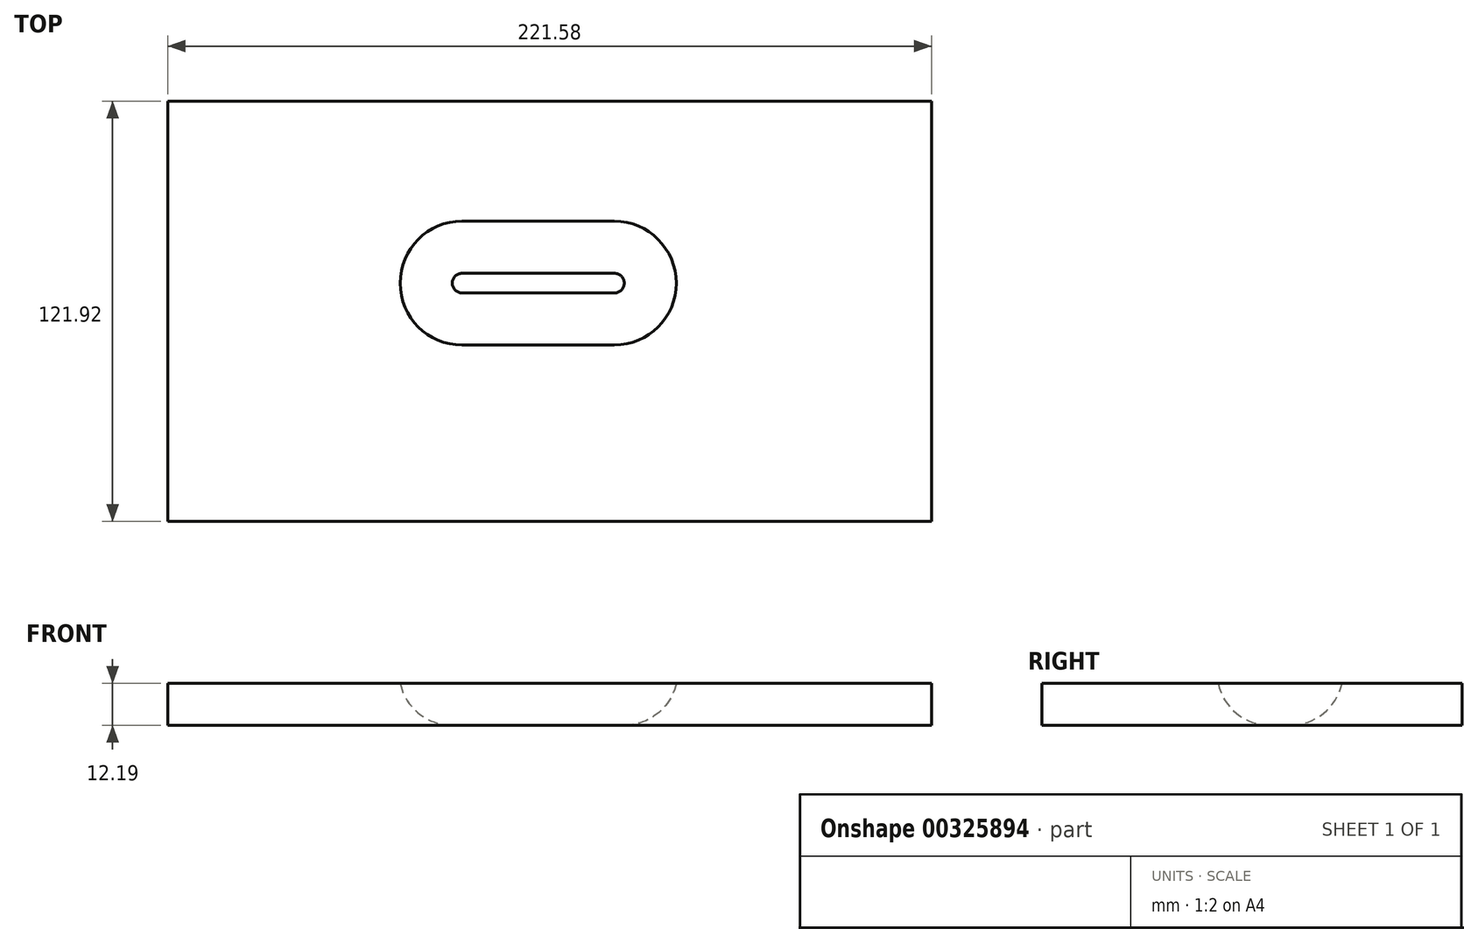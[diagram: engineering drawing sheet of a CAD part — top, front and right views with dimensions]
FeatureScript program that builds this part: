
annotation { "Feature Type Name" : "Feature", "Feature Type Description" : "" }
export const myFeature = defineFeature(function(context is Context, id is Id, definition is map)
    precondition{}
    {
        {
            var Q0;
            Q0=qCreatedBy(makeId("Top.planeOp"),FACE);
            var sketch = newSketch(context, id + "F0", { "sketchPlane" : qUnion([Q0])});
            skLineSegment(sketch, "E0.bottom", {"start": v(0, 0) * mm, "end": v(44.16, 0) * mm});
            skLineSegment(sketch, "E0.top", {"start": v(0, 36.63) * mm, "end": v(44.16, 36.63) * mm});
            skArc(sketch, "E1", {"start": v(0, 36.63) * mm, "mid": v(-18.32, 18.32) * mm, "end": v(0, 0) * mm});
            skArc(sketch, "E2", {"start": v(44.16, 0) * mm, "mid": v(62.47, 18.32) * mm, "end": v(44.16, 36.63) * mm});
            skSolve(sketch);
        }
        {
            var Q0;
            Q0=makeQuery(id+"F0.imprint","IMPRINT",FACE,{"disambiguationData":[TD([[makeQuery(id+"F0.imprint","IMPRINT",EDGE,{"derivedFrom":sQuery(id+"F0.wireOp",EDGE,"E0.bottom")}),1.0]])]});
            extrude(context, id + "F1", {"entities" : qUnion([Q0]), "depth" : 15.54 * mm});
        }
        {
            var Q0;
            Q0=makeQuery(id+"F1.opExtrude","CAP_EDGE",EDGE,{"disambiguationData":[OSD([sQuery(id+"F0.wireOp",EDGE,"E0.top")])],"isStart":true});
            var Q1;
            Q1=makeQuery(id+"F1.opExtrude","CAP_EDGE",EDGE,{"disambiguationData":[OSD([sQuery(id+"F0.wireOp",EDGE,"E2")])],"isStart":true});
            var Q2;
            Q2=makeQuery(id+"F1.opExtrude","CAP_EDGE",EDGE,{"disambiguationData":[OSD([sQuery(id+"F0.wireOp",EDGE,"E1")])],"isStart":true});
            fillet(context, id + "F2", {"entities" : qUnion([Q0, Q1, Q2]), "radius" : 15.45 * mm, "tangentPropagation" : true, "allowEdgeOverflow" : false});
        }
        {
            var Q0;
            Q0=qCreatedBy(makeId("Top.planeOp"),FACE);
            var sketch = newSketch(context, id + "F3", { "sketchPlane" : qUnion([Q0])});
            skLineSegment(sketch, "E3.bottom", {"start": v(-85.4, -50.8) * mm, "end": v(136.2, -50.8) * mm});
            skLineSegment(sketch, "E3.top", {"start": v(-85.4, 71.12) * mm, "end": v(136.2, 71.12) * mm});
            skLineSegment(sketch, "E3.left", {"start": v(-85.4, -50.8) * mm, "end": v(-85.4, 71.12) * mm});
            skLineSegment(sketch, "E3.right", {"start": v(136.2, -50.8) * mm, "end": v(136.2, 71.12) * mm});
            skSolve(sketch);
        }
        {
            var Q0;
            Q0=makeQuery(id+"F3.imprint","IMPRINT",FACE,{"disambiguationData":[TD([[makeQuery(id+"F3.imprint","IMPRINT",EDGE,{"derivedFrom":sQuery(id+"F3.wireOp",EDGE,"E3.bottom")}),1.0]])]});
            extrude(context, id + "F4", {"entities" : qUnion([Q0]), "depth" : 12.2 * mm});
        }
        {
            var Q0;
            Q0=makeQuery(id+"F1.opExtrude","SWEPT_BODY",BODY,{"disambiguationData":[OSD([sQuery(id+"F0.wireOp",EDGE,"E0.bottom"),sQuery(id+"F0.wireOp",EDGE,"E0.top"),sQuery(id+"F0.wireOp",EDGE,"E1"),sQuery(id+"F0.wireOp",EDGE,"E2")])]});
            var Q1;
            Q1=makeQuery(id+"F4.opExtrude","SWEPT_BODY",BODY,{"disambiguationData":[OSD([sQuery(id+"F3.wireOp",EDGE,"E3.bottom"),sQuery(id+"F3.wireOp",EDGE,"E3.top"),sQuery(id+"F3.wireOp",EDGE,"E3.left"),sQuery(id+"F3.wireOp",EDGE,"E3.right")])]});
            booleanBodies(context, id + "F5", {"operationType" : BooleanOperationType.SUBTRACTION, "tools" : qUnion([Q0]), "targets" : qUnion([Q1])});
        }
        {
            var Q0;
            Q0=makeQuery(id+"F4.opExtrude","SWEPT_BODY",BODY,{"disambiguationData":[OSD([sQuery(id+"F3.wireOp",EDGE,"E3.bottom"),sQuery(id+"F3.wireOp",EDGE,"E3.top"),sQuery(id+"F3.wireOp",EDGE,"E3.left"),sQuery(id+"F3.wireOp",EDGE,"E3.right")])]});
            transform(context, id + "F6", {"entities" : qUnion([Q0]), "transformType" : TransformType.TRANSLATION_3D, "dx" : 0 * mm, "dy" : 0 * mm, "dz" : -2.74 * mm, "makeCopy" : false});
        }
    });
